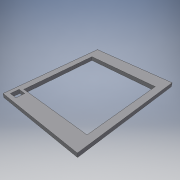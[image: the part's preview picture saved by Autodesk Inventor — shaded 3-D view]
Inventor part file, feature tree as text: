
AUTODESK INVENTOR PART (.ipt)
format: ipt  version: 2016 (Build 200138000, 138)  size: 111,104 bytes
history: native  units: in
note: dims shown in document units (in); Inventor stores cm internally (conversion verified against a paired STEP export)
features: extrude x3, sketch x3
ambient origin geometry x8: Origin, YZ Plane, XZ Plane, XY Plane, X Axis, Y Axis, Z Axis, Center Point
bodies: Solid1 (feature_tree)
feature tree (6):
  extrude  "Extrusion1"  Depth=16.0in
  extrude  "Extrusion2"  Depth=14.5in
  extrude  "Extrusion3"  Depth=1.0in TaperAngle=0.0deg
  sketch  "Sketch1"  dims[d0=20.0in d1=16.0in]
  sketch  "Sketch2"  dims[d2=0.75in d3=0.0in d4=14.5in]
  sketch  "Sketch3"  dims[d5=13.5in d6=1.0in d7=0.0in d9=0.75in d10=1.5in d11=1.0in d12=0.0in d13=1.5in d14=0.75in]
